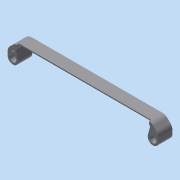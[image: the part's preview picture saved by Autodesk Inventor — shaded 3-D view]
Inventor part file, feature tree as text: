
AUTODESK INVENTOR PART (.ipt)
format: ipt  version: 2016 (Build 200138000, 138)  size: 166,912 bytes
history: native  units: in
note: dims shown in document units (in); Inventor stores cm internally (conversion verified against a paired STEP export)
features: extrude x3, sketch x3, projected_geometry x2
ambient origin geometry x8: Origin, YZ Plane, XZ Plane, XY Plane, X Axis, Y Axis, Z Axis, Center Point
bodies: Body1 (feature_tree)
feature tree (8):
  extrude  "Extrusion2"  Depth=0.125in
  extrude  "Extrusion3"  Depth=0.125in
  extrude  "Extrusion4"  Depth=0.095in
  sketch  "Sketch1"  dims[d7=0.125in d8=0.125in]
  sketch  "Sketch4"  dims[d9=0.125in d10=0.125in]
  projected_geometry  "Projected Loop1"
  sketch  "Sketch5"  dims[d11=0.237in d12=0.095in d13=0.063in d14=0.02in d15=75.0deg d16=2.5in d19=0.12in d20=0.12in d21=0.21in d22=0.0in d24=0.07in d25=0.07in d26=0.04in d27=0.0in d28=0.12in d29=0.041in d30=0.05in d31=0.0in d32=0.0in]
  projected_geometry  "Projected Loop2"
